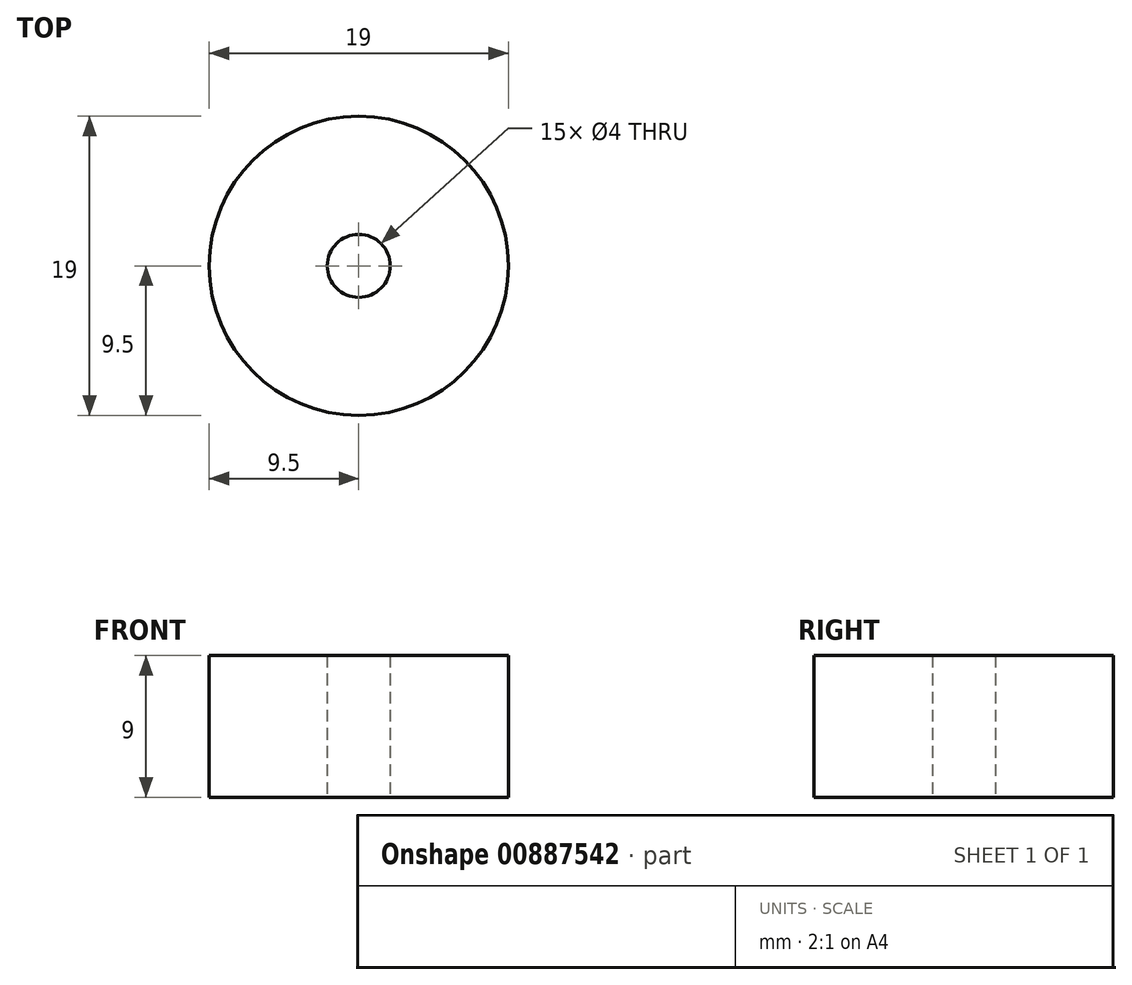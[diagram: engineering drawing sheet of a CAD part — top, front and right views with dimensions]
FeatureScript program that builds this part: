
annotation { "Feature Type Name" : "Feature", "Feature Type Description" : "" }
export const myFeature = defineFeature(function(context is Context, id is Id, definition is map)
    precondition{}
    {
        {
            var Q0;
            Q0=qCreatedBy(makeId("Top.planeOp"),FACE);
            var sketch = newSketch(context, id + "F0", { "sketchPlane" : qUnion([Q0])});
            skCircle(sketch, "E0", {"center": v(0, 0) * mm, "radius": 9.5 * mm});
            skCircle(sketch, "E1", {"center": v(0, 0) * mm, "radius": 2 * mm});
            skSolve(sketch);
        }
        {
            var Q0;
            Q0 = qSketchRegion(id + "F0", true);
            var Q1;
            Q1=makeQuery(id+"F0.imprint","IMPRINT",FACE,{"disambiguationData":[TD([[makeQuery(id+"F0.imprint","IMPRINT",EDGE,{"derivedFrom":sQuery(id+"F0.wireOp",EDGE,"E0")}),1.0]])]});
            extrude(context, id + "F1", {"entities" : qUnion([Q0, Q1]), "depth" : 9 * mm, "offsetDistance" : 25.4 * mm});
        }
    });
